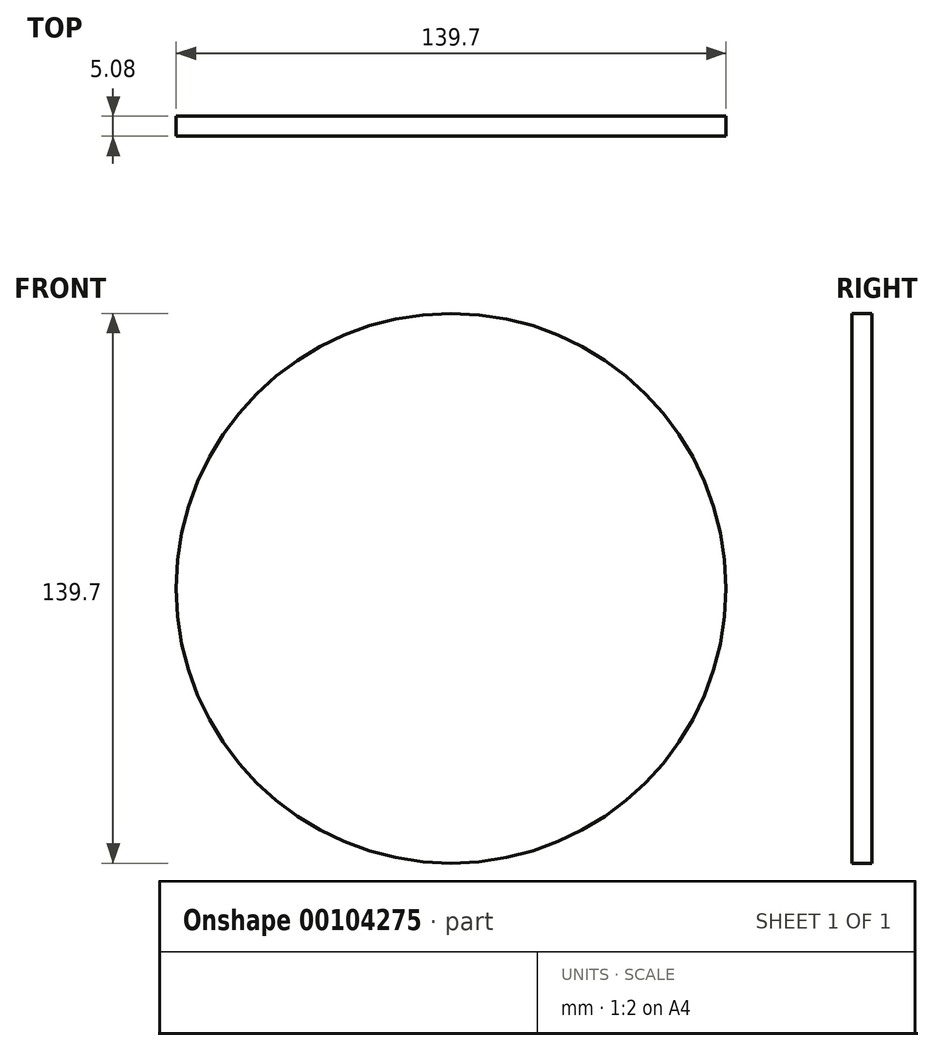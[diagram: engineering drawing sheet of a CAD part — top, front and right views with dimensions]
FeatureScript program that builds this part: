
annotation { "Feature Type Name" : "Feature", "Feature Type Description" : "" }
export const myFeature = defineFeature(function(context is Context, id is Id, definition is map)
    precondition{}
    {
        {
            var Q0;
            Q0=qCreatedBy(makeId("Front.planeOp"),FACE);
            var sketch = newSketch(context, id + "F0", { "sketchPlane" : qUnion([Q0])});
            skCircle(sketch, "E0", {"center": v(0, 0) * mm, "radius": 69.85 * mm});
            skSolve(sketch);
        }
        {
            var Q0;
            Q0=makeQuery(id+"F0.imprint","IMPRINT",FACE,{"disambiguationData":[TD([[makeQuery(id+"F0.imprint","IMPRINT",EDGE,{"derivedFrom":sQuery(id+"F0.wireOp",EDGE,"E0")}),1.0]])]});
            extrude(context, id + "F1", {"entities" : qUnion([Q0]), "depth" : 5.08 * mm});
        }
    });
